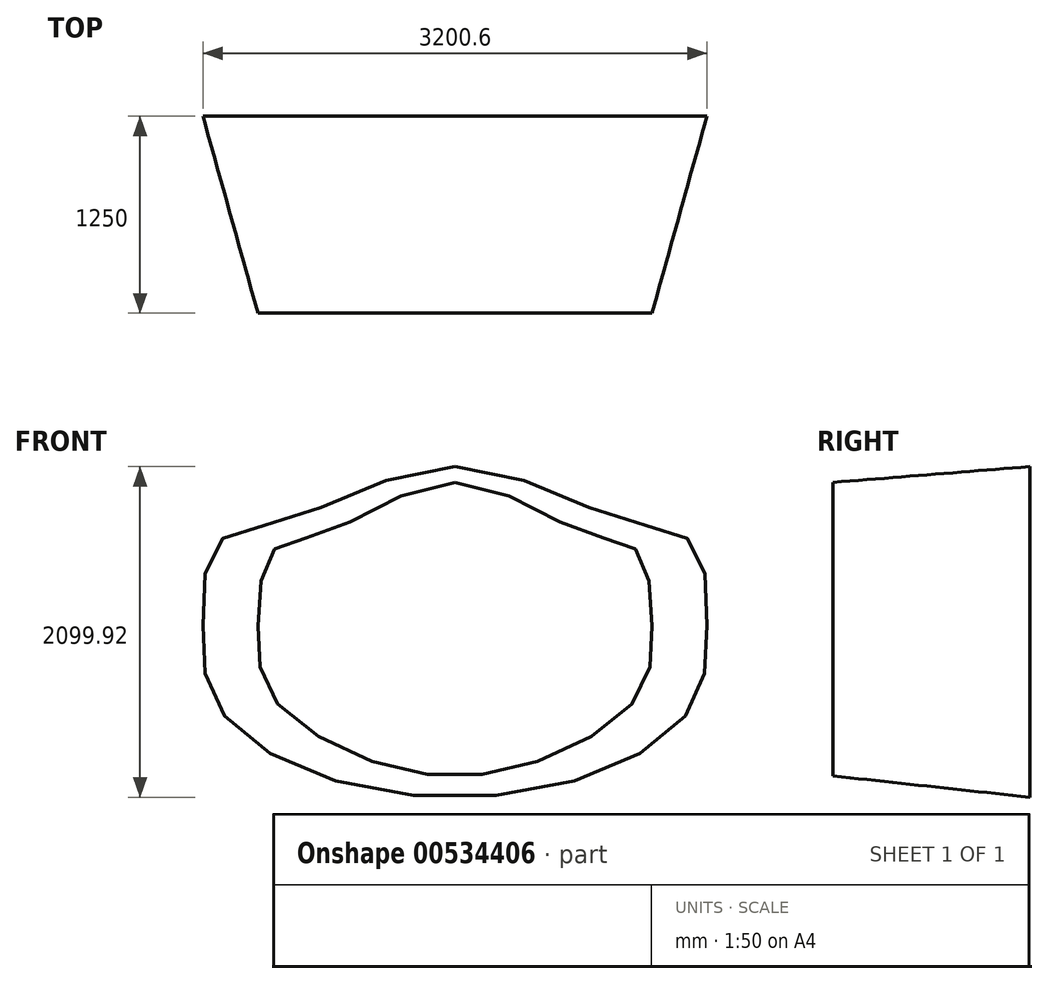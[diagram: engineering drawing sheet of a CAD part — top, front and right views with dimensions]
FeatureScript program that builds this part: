
annotation { "Feature Type Name" : "Feature", "Feature Type Description" : "" }
export const myFeature = defineFeature(function(context is Context, id is Id, definition is map)
    precondition{}
    {
        {
            var Q0;
            Q0=qCreatedBy(makeId("Front.planeOp"),FACE);
            var sketch = newSketch(context, id + "F0", { "sketchPlane" : qUnion([Q0])});
            skPoint(sketch, "E0.middle", {"position": v(0, 0) * mm});
            skFitSpline(sketch, "E1", {"points": [v(0, 1000) * mm, v(1060, 662.5) * mm, v(1517.6, 506.84) * mm, v(1600, 0) * mm, v(1517.6, -506.84) * mm, v(750, -1000) * mm, v(-750, -1000) * mm, v(-1517.6, -506.84) * mm, v(-1600, 0) * mm, v(-1517.6, 506.84) * mm, v(-1060, 662.5) * mm, v(0, 1000) * mm]});
            skSolve(sketch);
        }
        {
            var Q0;
            Q0=qCreatedBy(makeId("Front.planeOp"),FACE);
            cPlane(context, id + "F1", {"entities" : qUnion([Q0]), "cplaneType" : CPlaneType.OFFSET, "offset" : 1250 * mm, "width" : 150 * mm, "height" : 150 * mm});
        }
        {
            var Q0;
            Q0=qCreatedBy(id+"F1.planeOp",FACE);
            var sketch = newSketch(context, id + "F2", { "sketchPlane" : qUnion([Q0])});
            skPoint(sketch, "E2.middle", {"position": v(0, 0) * mm});
            skFitSpline(sketch, "E3", {"points": [v(0, 900) * mm, v(811.53, 584.3) * mm, v(1162.87, 458.52) * mm, v(1250, 0) * mm, v(1162.87, -458.52) * mm, v(435.89, -900) * mm, v(-435.89, -900) * mm, v(-1162.87, -458.52) * mm, v(-1250, 0) * mm, v(-1162.87, 458.52) * mm, v(-811.53, 584.3) * mm, v(0, 900) * mm]});
            skSolve(sketch);
        }
        {
            var Q0;
            Q0=makeQuery(id+"F2.imprint","IMPRINT",FACE,{"disambiguationData":[TD([[makeQuery(id+"F2.imprint","IMPRINT",EDGE,{"derivedFrom":sQuery(id+"F2.wireOp",EDGE,"E3")}),-1.0]])]});
            var Q1;
            Q1=makeQuery(id+"F0.imprint","IMPRINT",FACE,{"disambiguationData":[TD([[makeQuery(id+"F0.imprint","IMPRINT",EDGE,{"derivedFrom":sQuery(id+"F0.wireOp",EDGE,"E1")}),-1.0]])]});
            loft(context, id + "F3", {"sheetProfilesArray" : [{ "sheetProfileEntities" : qUnion([Q0]) }, { "sheetProfileEntities" : qUnion([Q1]) }]});
        }
    });
